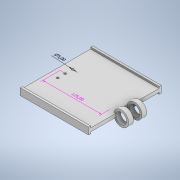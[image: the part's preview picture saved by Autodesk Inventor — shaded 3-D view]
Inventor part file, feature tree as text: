
AUTODESK INVENTOR PART (.ipt)
format: ipt  version: 2021 (Build 250183000, 183)  size: 219,648 bytes
history: native  units: mm
features: extrude x8, sketch x8, other x3, thicken_offset x1
ambient origin geometry x8: Origin, YZ Plane, XZ Plane, XY Plane, X Axis, Y Axis, Z Axis, Center Point
bodies: Solid1 (feature_tree)
feature tree (20):
  other  "Annotations"
  extrude  "Extrusion1"  Depth=4.0mm
  extrude  "Extrusion2"  Depth=160.0mm
  extrude  "Extrusion3"  Depth=4.0mm
  extrude  "Extrusion4"  Depth=16.0mm
  extrude  "Extrusion5"  Depth=4.0mm
  extrude  "Extrusion6"  Depth=16.0mm
  thicken_offset  "Thicken1"
  extrude  "Extrusion7"  Depth=160.0mm TaperAngle=0.0deg
  extrude  "Extrusion8"  Depth=10.0mm
  sketch  "Sketch1"  dims[d0=4.0mm d1=80.0mm]
  sketch  "Sketch2"  dims[d2=8.0mm d3=160.0mm]
  sketch  "Sketch3"  dims[d4=8.0mm d5=4.0mm]
  sketch  "Sketch4"  dims[d6=5.0mm d7=16.0mm]
  sketch  "Sketch5"  dims[d8=5.0mm d9=4.0mm]
  sketch  "Sketch6"  dims[d10=5.0mm d11=16.0mm]
  sketch  "Sketch7"  dims[d12=5.0mm d13=160.0mm d14=0.0mm]
  sketch  "Sketch8"  dims[d15=80.0mm d16=10.0mm d17=5.0mm d18=17.5mm d19=17.5mm d20=5.0mm d21=5.0mm d22=10.0mm d23=0.0mm d24=20.0mm d25=8.0mm d26=0.0mm d27=20.0mm d28=17.5mm d29=17.5mm d30=5.0mm d31=5.0mm d32=5.0mm d33=8.0mm d34=0.0mm d35=145.0mm d36=21.0mm d37=42.0mm d38=10.0mm d39=0.0mm d40=10.0mm d41=40.0mm d42=2.0mm d43=10.0mm d44=0.0mm d49=10.0mm d50=10.0mm d51=17.5mm d53=4.0mm d55=10.0mm d56=25.0mm d57=42.0mm d58=0.0mm d59=11.0mm d60=20.0mm d61=50.0mm d62=0.0mm d45=5.103633mm d46=125.0mm d47=12.519352mm d48=5.0mm]
  other  "Linear Dimension 1"
  other  "Diameter Dimension 1"
